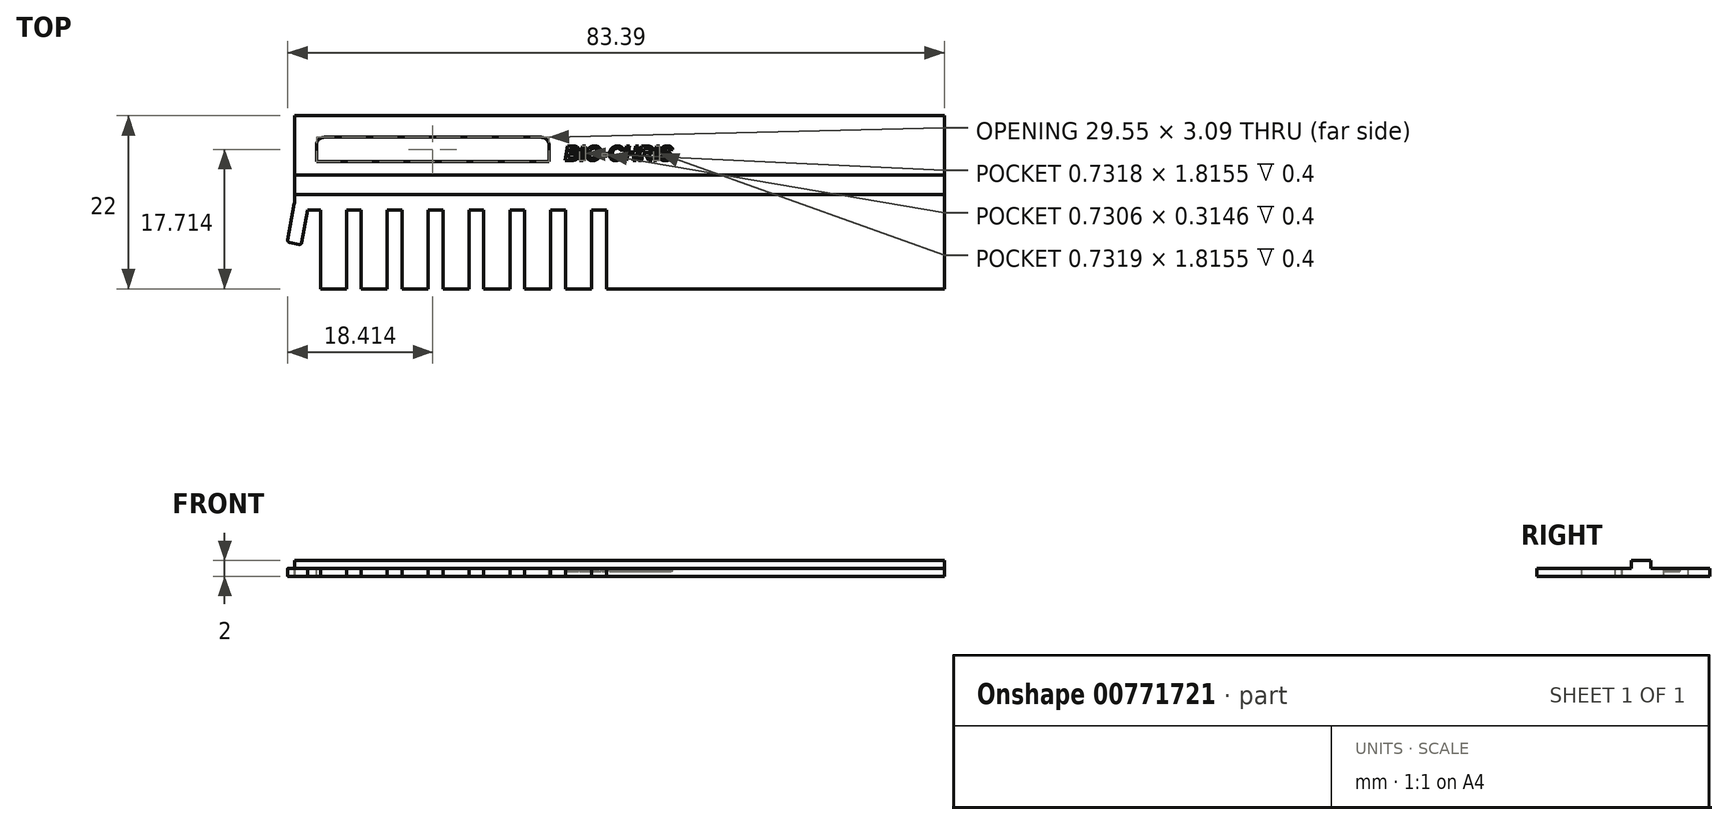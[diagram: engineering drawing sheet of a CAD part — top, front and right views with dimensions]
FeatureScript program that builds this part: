
annotation { "Feature Type Name" : "Feature", "Feature Type Description" : "" }
export const myFeature = defineFeature(function(context is Context, id is Id, definition is map)
    precondition{}
    {
        {
            var Q0;
            Q0=qCreatedBy(makeId("Top.planeOp"),FACE);
            var sketch = newSketch(context, id + "F0", { "sketchPlane" : qUnion([Q0])});
            skLineSegment(sketch, "E0.bottom", {"start": v(-41.25, 11) * mm, "end": v(41.25, 11) * mm});
            skLineSegment(sketch, "E0.top", {"start": v(-41.25, -11) * mm, "end": v(41.25, -11) * mm});
            skLineSegment(sketch, "E0.left", {"start": v(-41.25, 11) * mm, "end": v(-41.25, -11) * mm});
            skLineSegment(sketch, "E0.right", {"start": v(41.25, 11) * mm, "end": v(41.25, -11) * mm});
            skPoint(sketch, "E0.middle", {"position": v(0, 0) * mm});
            skSolve(sketch);
        }
        {
            var Q0;
            Q0 = qSketchRegion(id + "F0", true);
            extrude(context, id + "F1", {"entities" : qUnion([Q0]), "depth" : 1 * mm, "offsetDistance" : 25 * mm});
        }
        {
            var Q0;
            Q0=makeQuery(id+"F1.opExtrude","CAP_FACE",FACE,{"disambiguationData":[OSD([sQuery(id+"F0.wireOp",EDGE,"E0.bottom"),sQuery(id+"F0.wireOp",EDGE,"E0.top"),sQuery(id+"F0.wireOp",EDGE,"E0.left"),sQuery(id+"F0.wireOp",EDGE,"E0.right")])],"isStart":false});
            var sketch = newSketch(context, id + "F2", { "sketchPlane" : qUnion([Q0])});
            skLineSegment(sketch, "E1.bottom", {"start": v(-41.25, -11) * mm, "end": v(-38, -11) * mm});
            skLineSegment(sketch, "E1.top", {"start": v(-41.25, -1) * mm, "end": v(-38, -1) * mm});
            skLineSegment(sketch, "E1.left", {"start": v(-41.25, -11) * mm, "end": v(-41.25, -1) * mm});
            skLineSegment(sketch, "E1.right", {"start": v(-38, -11) * mm, "end": v(-38, -1) * mm});
            skSolve(sketch);
        }
        {
            var Q0;
            Q0 = qSketchRegion(id + "F2", true);
            extrude(context, id + "F3", {"entities" : qUnion([Q0]), "operationType" : NewBodyOperationType.REMOVE, "oppositeDirection" : true, "depth" : 1 * mm, "offsetDistance" : 25 * mm});
        }
        {
            var Q0;
            Q0=makeQuery(id+"F1.opExtrude","CAP_FACE",FACE,{"disambiguationData":[OSD([sQuery(id+"F0.wireOp",EDGE,"E0.bottom"),sQuery(id+"F0.wireOp",EDGE,"E0.top"),sQuery(id+"F0.wireOp",EDGE,"E0.left"),sQuery(id+"F0.wireOp",EDGE,"E0.right")])],"isStart":false});
            var sketch = newSketch(context, id + "F4", { "sketchPlane" : qUnion([Q0])});
            skLineSegment(sketch, "E2.bottom", {"start": v(-34.7, -11) * mm, "end": v(-32.81, -11) * mm});
            skLineSegment(sketch, "E2.top", {"start": v(-34.7, -1) * mm, "end": v(-32.81, -1) * mm});
            skLineSegment(sketch, "E2.left", {"start": v(-34.7, -11) * mm, "end": v(-34.7, -1) * mm});
            skLineSegment(sketch, "E2.right", {"start": v(-32.81, -11) * mm, "end": v(-32.81, -1) * mm});
            skLineSegment(sketch, "E3.bottom", {"start": v(-29.5, -11) * mm, "end": v(-27.62, -11) * mm});
            skLineSegment(sketch, "E3.top", {"start": v(-29.5, -1) * mm, "end": v(-27.62, -1) * mm});
            skLineSegment(sketch, "E3.left", {"start": v(-29.5, -11) * mm, "end": v(-29.5, -1) * mm});
            skLineSegment(sketch, "E3.right", {"start": v(-27.62, -11) * mm, "end": v(-27.62, -1) * mm});
            skLineSegment(sketch, "E4.bottom", {"start": v(-24.32, -11) * mm, "end": v(-22.43, -11) * mm});
            skLineSegment(sketch, "E4.top", {"start": v(-24.32, -1) * mm, "end": v(-22.43, -1) * mm});
            skLineSegment(sketch, "E4.left", {"start": v(-24.32, -11) * mm, "end": v(-24.32, -1) * mm});
            skLineSegment(sketch, "E4.right", {"start": v(-22.43, -11) * mm, "end": v(-22.43, -1) * mm});
            skLineSegment(sketch, "E5.bottom", {"start": v(-19.13, -11) * mm, "end": v(-17.24, -11) * mm});
            skLineSegment(sketch, "E5.top", {"start": v(-19.13, -1) * mm, "end": v(-17.24, -1) * mm});
            skLineSegment(sketch, "E5.left", {"start": v(-19.13, -11) * mm, "end": v(-19.13, -1) * mm});
            skLineSegment(sketch, "E5.right", {"start": v(-17.24, -11) * mm, "end": v(-17.24, -1) * mm});
            skLineSegment(sketch, "E6.bottom", {"start": v(-13.94, -11) * mm, "end": v(-12.05, -11) * mm});
            skLineSegment(sketch, "E6.top", {"start": v(-13.94, -1) * mm, "end": v(-12.05, -1) * mm});
            skLineSegment(sketch, "E6.left", {"start": v(-13.94, -11) * mm, "end": v(-13.94, -1) * mm});
            skLineSegment(sketch, "E6.right", {"start": v(-12.05, -11) * mm, "end": v(-12.05, -1) * mm});
            skLineSegment(sketch, "E7.bottom", {"start": v(-8.75, -11) * mm, "end": v(-6.86, -11) * mm});
            skLineSegment(sketch, "E7.top", {"start": v(-8.75, -1) * mm, "end": v(-6.86, -1) * mm});
            skLineSegment(sketch, "E7.left", {"start": v(-8.75, -11) * mm, "end": v(-8.75, -1) * mm});
            skLineSegment(sketch, "E7.right", {"start": v(-6.86, -11) * mm, "end": v(-6.86, -1) * mm});
            skLineSegment(sketch, "E8.bottom", {"start": v(-3.56, -11) * mm, "end": v(-1.67, -11) * mm});
            skLineSegment(sketch, "E8.top", {"start": v(-3.56, -1) * mm, "end": v(-1.67, -1) * mm});
            skLineSegment(sketch, "E8.left", {"start": v(-3.56, -11) * mm, "end": v(-3.56, -1) * mm});
            skLineSegment(sketch, "E8.right", {"start": v(-1.67, -11) * mm, "end": v(-1.67, -1) * mm});
            skSolve(sketch);
        }
        {
            var Q0;
            Q0 = qSketchRegion(id + "F4", true);
            extrude(context, id + "F5", {"entities" : qUnion([Q0]), "operationType" : NewBodyOperationType.REMOVE, "oppositeDirection" : true, "depth" : 1 * mm, "offsetDistance" : 25 * mm});
        }
        {
            var Q0;
            Q0=qCreatedBy(makeId("Top.planeOp"),FACE);
            var sketch = newSketch(context, id + "F6", { "sketchPlane" : qUnion([Q0])});
            skLineSegment(sketch, "E9.bottom", {"start": v(-41.32, -0.16) * mm, "end": v(-39.55, -0.48) * mm});
            skLineSegment(sketch, "E9.top", {"start": v(-41.9, -5.14) * mm, "end": v(-40.71, -5.35) * mm});
            skLineSegment(sketch, "E9.left", {"start": v(-41.32, -0.16) * mm, "end": v(-42.14, -4.8) * mm});
            skLineSegment(sketch, "E9.right", {"start": v(-39.55, -0.48) * mm, "end": v(-40.36, -5.1) * mm});
            skPoint(sketch, "E10.visualSharp", {"position": v(-40.42, -5.4) * mm});
            skArc(sketch, "E10.filletArc", {"start": v(-40.71, -5.35) * mm, "mid": v(-40.49, -5.3) * mm, "end": v(-40.36, -5.1) * mm});
            skPoint(sketch, "E11.visualSharp", {"position": v(-42.19, -5.09) * mm});
            skArc(sketch, "E11.filletArc", {"start": v(-42.14, -4.8) * mm, "mid": v(-42.09, -5.02) * mm, "end": v(-41.9, -5.14) * mm});
            skSolve(sketch);
        }
        {
            var Q0;
            Q0 = qSketchRegion(id + "F6", true);
            extrude(context, id + "F7", {"entities" : qUnion([Q0]), "operationType" : NewBodyOperationType.ADD, "depth" : 1 * mm, "offsetDistance" : 25 * mm});
        }
        {
            var Q0;
            {var subQ0=sQuery(id+"F6.wireOp",EDGE,"E11.filletArc");var subQ1=sQuery(id+"F6.wireOp",EDGE,"E10.filletArc");var subQ2=sQuery(id+"F6.wireOp",EDGE,"E9.right");var subQ3=sQuery(id+"F6.wireOp",EDGE,"E9.left");var subQ4=sQuery(id+"F6.wireOp",EDGE,"E9.top");var subQ5=sQuery(id+"F6.wireOp",EDGE,"E9.bottom");Q0=makeQuery(id+"FNUQPgyaXuvFqtC_1.1.F7.boolean.opBoolean","MERGE",FACE,{"derivedFrom":[makeQuery(id+"F7.boolean.opBoolean","MERGE",FACE,{"derivedFrom":[makeQuery(id+"F1.opExtrude","CAP_FACE",FACE,{"disambiguationData":[OSD([sQuery(id+"F0.wireOp",EDGE,"E0.bottom"),sQuery(id+"F0.wireOp",EDGE,"E0.top"),sQuery(id+"F0.wireOp",EDGE,"E0.left"),sQuery(id+"F0.wireOp",EDGE,"E0.right")])],"isStart":false}),makeQuery(id+"F7.opExtrude","CAP_FACE",FACE,{"disambiguationData":[OSD([subQ5,subQ4,subQ3,subQ2,subQ1,subQ0])],"isStart":false})]}),makeQuery(id+"FNUQPgyaXuvFqtC_1.1.F7.opExtrude","CAP_FACE",FACE,{"disambiguationData":[OSD([subQ5,subQ4,subQ3,subQ2,subQ1,subQ0])],"isStart":false})]});}
            var sketch = newSketch(context, id + "F8", { "sketchPlane" : qUnion([Q0])});
            skLineSegment(sketch, "E12.bottom", {"start": v(-41.25, 1) * mm, "end": v(41.25, 1) * mm});
            skLineSegment(sketch, "E12.top", {"start": v(-41.25, 3.46) * mm, "end": v(41.25, 3.46) * mm});
            skLineSegment(sketch, "E12.left", {"start": v(-41.25, 1) * mm, "end": v(-41.25, 3.46) * mm});
            skLineSegment(sketch, "E12.right", {"start": v(41.25, 1) * mm, "end": v(41.25, 3.46) * mm});
            skSolve(sketch);
        }
        {
            var Q0;
            Q0 = qSketchRegion(id + "F8", true);
            extrude(context, id + "F9", {"entities" : qUnion([Q0]), "operationType" : NewBodyOperationType.ADD, "depth" : 1 * mm, "offsetDistance" : 25 * mm});
        }
        {
            var Q0;
            {var subQ0=sQuery(id+"F0.wireOp",EDGE,"E0.left");var subQ1=sQuery(id+"F0.wireOp",EDGE,"E0.right");var subQ2=sQuery(id+"F0.wireOp",EDGE,"E0.bottom");var subQ3=sQuery(id+"F6.wireOp",EDGE,"E11.filletArc");var subQ4=sQuery(id+"F6.wireOp",EDGE,"E10.filletArc");var subQ5=sQuery(id+"F6.wireOp",EDGE,"E9.right");var subQ6=sQuery(id+"F6.wireOp",EDGE,"E9.left");var subQ7=sQuery(id+"F6.wireOp",EDGE,"E9.top");var subQ8=sQuery(id+"F6.wireOp",EDGE,"E9.bottom");Q0=makeQuery(id+"F9.boolean.opBoolean","SPLIT",FACE,{"disambiguationData":[TD([makeQuery(id+"F1.opExtrude","SWEPT_FACE",FACE,{"disambiguationData":[OSD([subQ2])]})])],"derivedFrom":makeQuery(id+"FNUQPgyaXuvFqtC_1.1.F7.boolean.opBoolean","MERGE",FACE,{"derivedFrom":[makeQuery(id+"F7.boolean.opBoolean","MERGE",FACE,{"derivedFrom":[makeQuery(id+"F1.opExtrude","CAP_FACE",FACE,{"disambiguationData":[OSD([subQ2,sQuery(id+"F0.wireOp",EDGE,"E0.top"),subQ0,subQ1])],"isStart":false}),makeQuery(id+"F7.opExtrude","CAP_FACE",FACE,{"disambiguationData":[OSD([subQ8,subQ7,subQ6,subQ5,subQ4,subQ3])],"isStart":false})]}),makeQuery(id+"FNUQPgyaXuvFqtC_1.1.F7.opExtrude","CAP_FACE",FACE,{"disambiguationData":[OSD([subQ8,subQ7,subQ6,subQ5,subQ4,subQ3])],"isStart":false})]})});}
            var sketch = newSketch(context, id + "F10", { "sketchPlane" : qUnion([Q0])});
            skLineSegment(sketch, "E13.bottom", {"start": v(-38.5, 5.17) * mm, "end": v(-8.95, 5.17) * mm});
            skLineSegment(sketch, "E13.top", {"start": v(-37.5, 8.26) * mm, "end": v(-9.95, 8.26) * mm});
            skLineSegment(sketch, "E13.left", {"start": v(-38.5, 5.17) * mm, "end": v(-38.5, 7.26) * mm});
            skLineSegment(sketch, "E13.right", {"start": v(-8.95, 5.17) * mm, "end": v(-8.95, 7.26) * mm});
            skPoint(sketch, "E14.visualSharp", {"position": v(-38.5, 8.26) * mm});
            skArc(sketch, "E14.filletArc", {"start": v(-37.5, 8.26) * mm, "mid": v(-38.21, 7.96) * mm, "end": v(-38.5, 7.26) * mm});
            skPoint(sketch, "E15.visualSharp", {"position": v(-8.95, 8.26) * mm});
            skArc(sketch, "E15.filletArc", {"start": v(-8.95, 7.26) * mm, "mid": v(-9.24, 7.96) * mm, "end": v(-9.95, 8.26) * mm});
            skSolve(sketch);
        }
        {
            var Q0;
            Q0=makeQuery(id+"F10.imprint","IMPRINT",FACE,{"disambiguationData":[TD([[makeQuery(id+"F10.imprint","IMPRINT",EDGE,{"derivedFrom":sQuery(id+"F10.wireOp",EDGE,"E13.bottom")}),1.0]])]});
            extrude(context, id + "F11", {"entities" : qUnion([Q0]), "operationType" : NewBodyOperationType.REMOVE, "oppositeDirection" : true, "depth" : 1 * mm, "offsetDistance" : 25 * mm});
        }
        {
            var Q0;
            {var subQ0=sQuery(id+"F0.wireOp",EDGE,"E0.left");var subQ1=sQuery(id+"F0.wireOp",EDGE,"E0.right");var subQ2=sQuery(id+"F0.wireOp",EDGE,"E0.bottom");var subQ3=sQuery(id+"F6.wireOp",EDGE,"E11.filletArc");var subQ4=sQuery(id+"F6.wireOp",EDGE,"E10.filletArc");var subQ5=sQuery(id+"F6.wireOp",EDGE,"E9.right");var subQ6=sQuery(id+"F6.wireOp",EDGE,"E9.left");var subQ7=sQuery(id+"F6.wireOp",EDGE,"E9.top");var subQ8=sQuery(id+"F6.wireOp",EDGE,"E9.bottom");Q0=makeQuery(id+"F9.boolean.opBoolean","SPLIT",FACE,{"disambiguationData":[TD([makeQuery(id+"F1.opExtrude","SWEPT_FACE",FACE,{"disambiguationData":[OSD([subQ2])]})])],"derivedFrom":makeQuery(id+"FNUQPgyaXuvFqtC_1.1.F7.boolean.opBoolean","MERGE",FACE,{"derivedFrom":[makeQuery(id+"F7.boolean.opBoolean","MERGE",FACE,{"derivedFrom":[makeQuery(id+"F1.opExtrude","CAP_FACE",FACE,{"disambiguationData":[OSD([subQ2,sQuery(id+"F0.wireOp",EDGE,"E0.top"),subQ0,subQ1])],"isStart":false}),makeQuery(id+"F7.opExtrude","CAP_FACE",FACE,{"disambiguationData":[OSD([subQ8,subQ7,subQ6,subQ5,subQ4,subQ3])],"isStart":false})]}),makeQuery(id+"FNUQPgyaXuvFqtC_1.1.F7.opExtrude","CAP_FACE",FACE,{"disambiguationData":[OSD([subQ8,subQ7,subQ6,subQ5,subQ4,subQ3])],"isStart":false})]})});}
            var sketch = newSketch(context, id + "F12", { "sketchPlane" : qUnion([Q0])});
            skText(sketch, "E16", { "text": "BIO-CHRIS", "fontName": "Arimo-BoldItalic.ttf"});
            const initialGuessF12  = {"E16": [-0.007, 0.00532, 1, 0, 0.0019]};
            skSetInitialGuess(sketch, initialGuessF12);
            skSolve(sketch);
        }
        {
            var Q0;
            Q0 = qSketchRegion(id + "F12", true);
            extrude(context, id + "F13", {"entities" : qUnion([Q0]), "operationType" : NewBodyOperationType.REMOVE, "oppositeDirection" : true, "depth" : 0.4 * mm, "offsetDistance" : 25 * mm});
        }
    });
